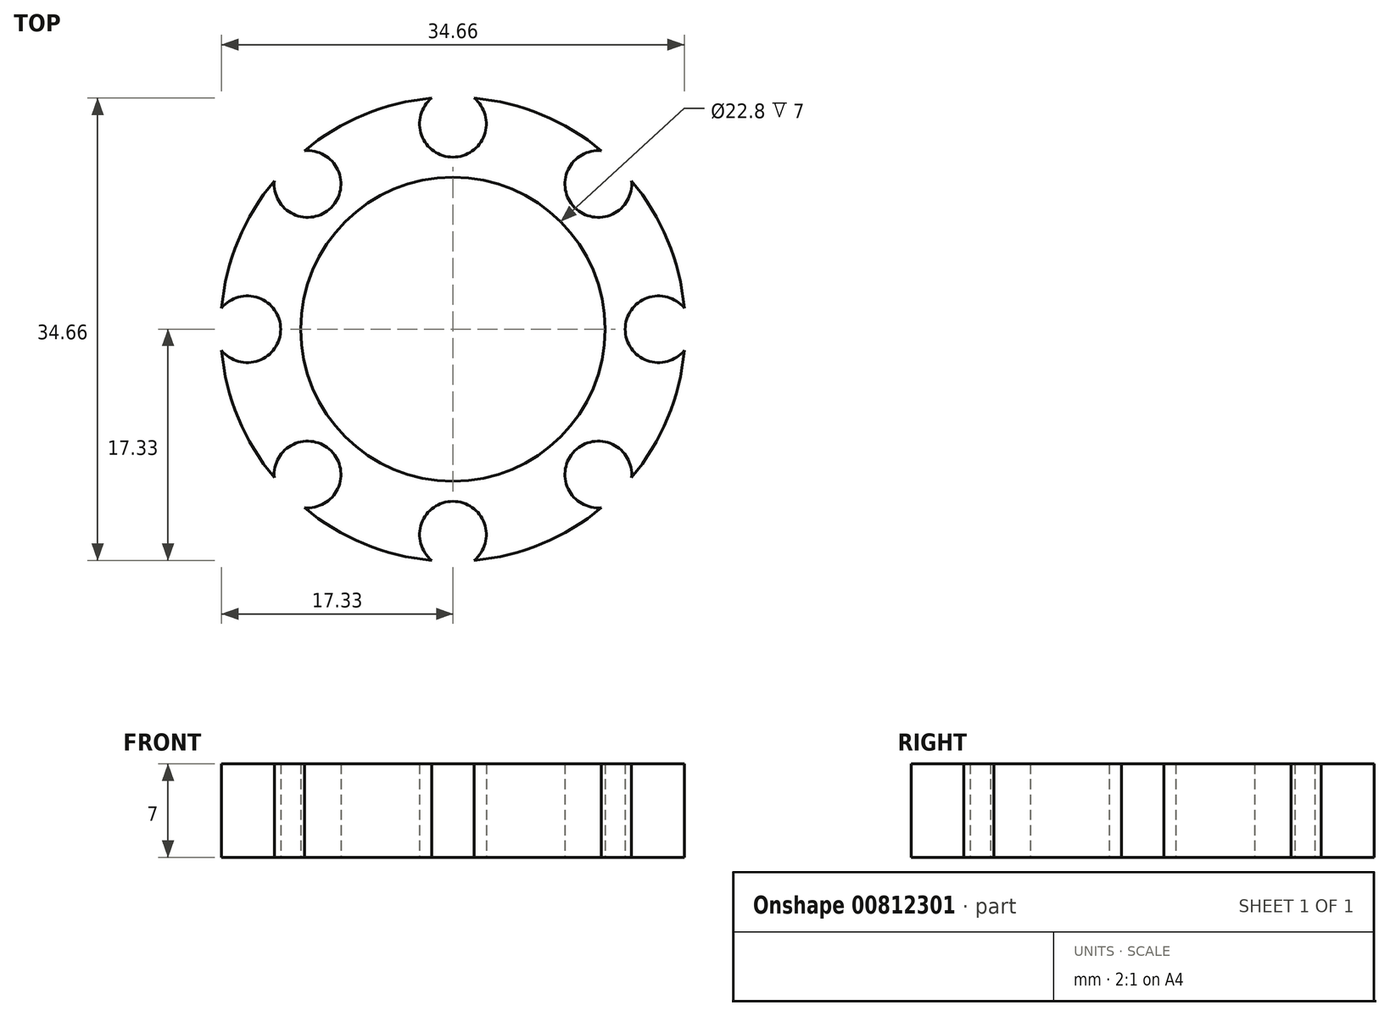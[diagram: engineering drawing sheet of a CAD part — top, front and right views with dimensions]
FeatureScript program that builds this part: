
annotation { "Feature Type Name" : "Feature", "Feature Type Description" : "" }
export const myFeature = defineFeature(function(context is Context, id is Id, definition is map)
    precondition{}
    {
        {
            var Q0;
            Q0=qCreatedBy(makeId("Top.planeOp"),FACE);
            var sketch = newSketch(context, id + "F0", { "sketchPlane" : qUnion([Q0])});
            skCircle(sketch, "E0", {"center": v(0, 0) * mm, "radius": 11.4 * mm});
            skCircle(sketch, "E1", {"center": v(0, 0) * mm, "radius": 17.4 * mm});
            skLineSegment(sketch, "E2", {"start": v(0, 0) * mm, "end": v(0, 26.16) * mm, "construction": true});
            skCircle(sketch, "E3", {"center": v(0, 15.4) * mm, "radius": 2.5 * mm});
            skCircle(sketch, "E4.1.0", {"center": v(-10.89, 10.89) * mm, "radius": 2.5 * mm});
            skCircle(sketch, "E4.2.0", {"center": v(-15.4, 0) * mm, "radius": 2.5 * mm});
            skCircle(sketch, "E4.3.0", {"center": v(-10.89, -10.89) * mm, "radius": 2.5 * mm});
            skCircle(sketch, "E4.4.0", {"center": v(0, -15.4) * mm, "radius": 2.5 * mm});
            skCircle(sketch, "E4.5.0", {"center": v(10.89, -10.89) * mm, "radius": 2.5 * mm});
            skCircle(sketch, "E4.6.0", {"center": v(15.4, 0) * mm, "radius": 2.5 * mm});
            skCircle(sketch, "E4.7.0", {"center": v(10.89, 10.89) * mm, "radius": 2.5 * mm});
            skSolve(sketch);
        }
        {
            var Q0;
            Q0=makeQuery(id+"F0.imprint","IMPRINT",FACE,{"disambiguationData":[TD([[makeQuery(id+"F0.imprint","IMPRINT",EDGE,{"derivedFrom":sQuery(id+"F0.wireOp",EDGE,"E0")}),-1.0]])]});
            extrude(context, id + "F1", {"entities" : qUnion([Q0]), "depth" : 7 * mm, "offsetDistance" : 25 * mm});
        }
    });
